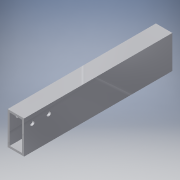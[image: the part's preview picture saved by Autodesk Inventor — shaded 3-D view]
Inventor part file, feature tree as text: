
AUTODESK INVENTOR PART (.ipt)
format: ipt  version: 2016 (Build 200138000, 138)  size: 113,664 bytes
history: native  units: in
note: dims shown in document units (in); Inventor stores cm internally (conversion verified against a paired STEP export)
features: extrude x2, sketch x2
ambient origin geometry x8: Origin, YZ Plane, XZ Plane, XY Plane, X Axis, Y Axis, Z Axis, Center Point
bodies: Solid1 (feature_tree)
feature tree (4):
  extrude  "Extrusion1"  Depth=2.0in
  extrude  "Extrusion2"  Depth=0.125in
  sketch  "Sketch1"  dims[d0=1.0in d1=2.0in]
  sketch  "Sketch2"  dims[d2=0.125in d3=0.125in d4=0.125in d5=0.125in d6=9.0in d7=0.0in d8=0.2656in d9=0.2656in d10=0.5in d11=0.5in d12=0.5in d13=1.5in d14=1.0in d15=0.0in]
